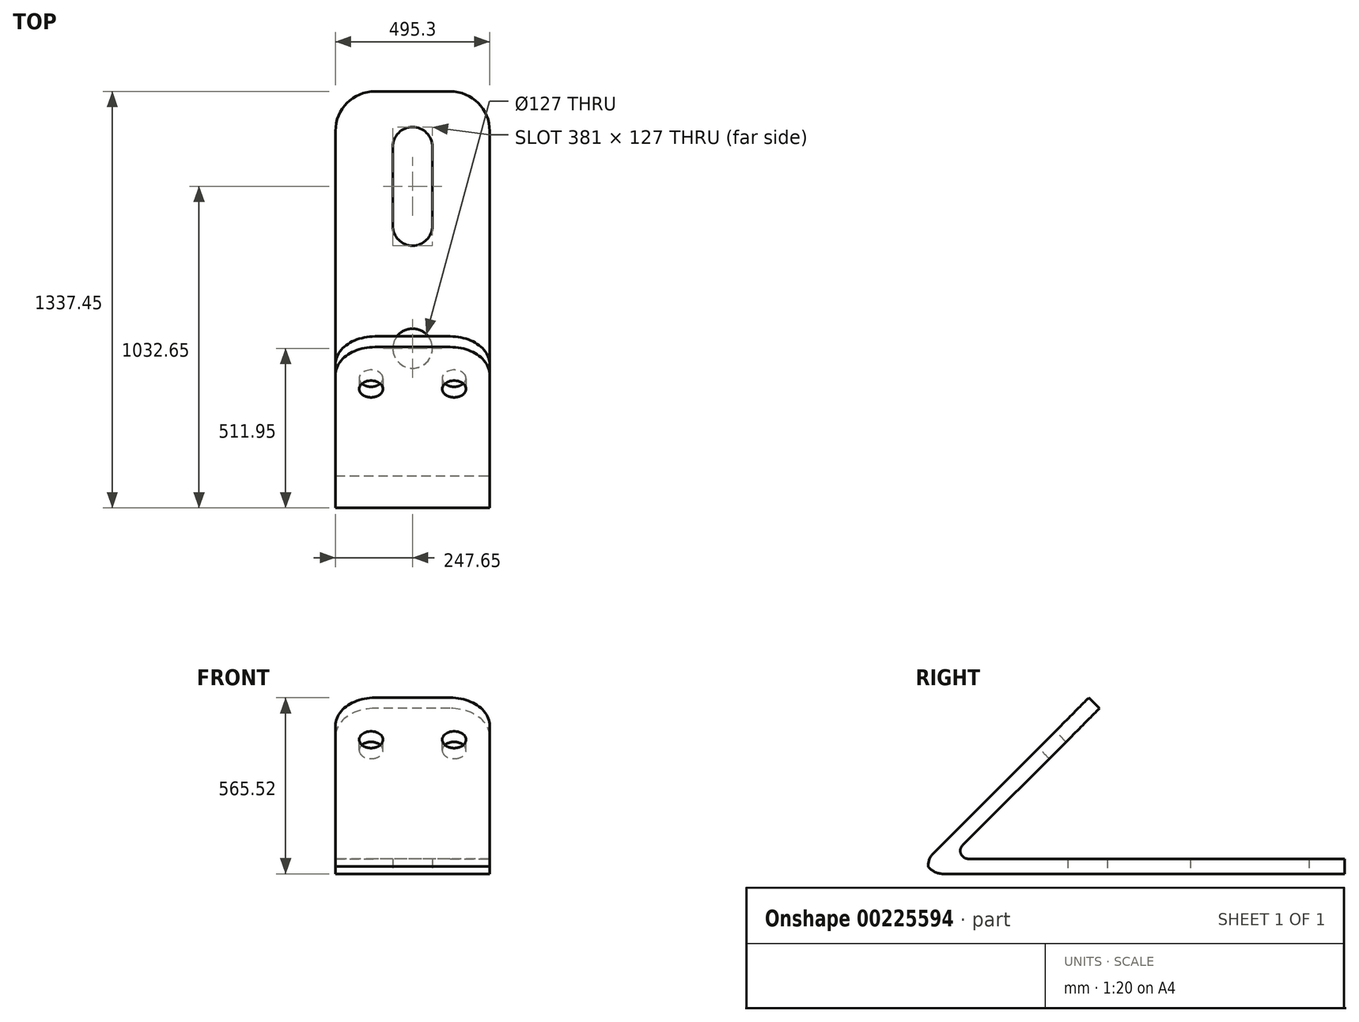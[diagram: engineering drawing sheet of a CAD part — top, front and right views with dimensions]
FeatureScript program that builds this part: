
annotation { "Feature Type Name" : "Feature", "Feature Type Description" : "" }
export const myFeature = defineFeature(function(context is Context, id is Id, definition is map)
    precondition{}
    {
        {
            var Q0;
            Q0=qCreatedBy(makeId("Right.planeOp"),FACE);
            var sketch = newSketch(context, id + "F0", { "sketchPlane" : qUnion([Q0])});
            skLineSegment(sketch, "E0", {"start": v(0, 0) * mm, "end": v(1270, 0) * mm});
            skLineSegment(sketch, "E1", {"start": v(1270, 0) * mm, "end": v(1270, 48.26) * mm});
            skLineSegment(sketch, "E2", {"start": v(1270, 48.26) * mm, "end": v(0, 48.26) * mm});
            skLineSegment(sketch, "E3", {"start": v(0, 48.26) * mm, "end": v(483.14, 531.4) * mm});
            skLineSegment(sketch, "E4", {"start": v(483.14, 531.4) * mm, "end": v(449.01, 565.52) * mm});
            skLineSegment(sketch, "E5", {"start": v(449.01, 565.52) * mm, "end": v(0, 116.5) * mm});
            skLineSegment(sketch, "E6", {"start": v(0, 116.5) * mm, "end": v(-67.45, 49.06) * mm});
            skLineSegment(sketch, "E7", {"start": v(-67.45, 49.06) * mm, "end": v(-67.45, 0) * mm});
            skLineSegment(sketch, "E8", {"start": v(-67.45, 0) * mm, "end": v(0, 0) * mm});
            skSolve(sketch);
        }
        {
            var Q0;
            Q0 = qSketchRegion(id + "F0", true);
            extrude(context, id + "F1", {"entities" : qUnion([Q0]), "endBound" : BoundingType.SYMMETRIC, "depth" : 495.3 * mm});
        }
        {
            var Q0;
            Q0=makeQuery(id+"F1.opExtrude","CAP_EDGE",EDGE,{"disambiguationData":[OSD([sQuery(id+"F0.wireOp",EDGE,"E4")])],"isStart":false});
            var Q1;
            Q1=makeQuery(id+"F1.opExtrude","CAP_EDGE",EDGE,{"disambiguationData":[OSD([sQuery(id+"F0.wireOp",EDGE,"E4")])],"isStart":true});
            var Q2;
            Q2=makeQuery(id+"F1.opExtrude","CAP_EDGE",EDGE,{"disambiguationData":[OSD([sQuery(id+"F0.wireOp",EDGE,"E1")])],"isStart":false});
            var Q3;
            Q3=makeQuery(id+"F1.opExtrude","CAP_EDGE",EDGE,{"disambiguationData":[OSD([sQuery(id+"F0.wireOp",EDGE,"E1")])],"isStart":true});
            fillet(context, id + "F2", {"entities" : qUnion([Q0, Q1, Q2, Q3]), "radius" : 127 * mm, "tangentPropagation" : true, "allowEdgeOverflow" : false});
        }
        {
            var Q0;
            Q0=makeQuery(id+"F1.opExtrude","SWEPT_EDGE",EDGE,{"disambiguationData":[OSD([sQuery(id+"F0.wireOp",EDGE,"E2"),sQuery(id+"F0.wireOp",EDGE,"E3")])]});
            fillet(context, id + "F3", {"entities" : qUnion([Q0]), "radius" : 25.4 * mm, "tangentPropagation" : true, "allowEdgeOverflow" : false});
        }
        {
            var Q0;
            Q0=makeQuery(id+"F1.opExtrude","SWEPT_EDGE",EDGE,{"disambiguationData":[OSD([sQuery(id+"F0.wireOp",EDGE,"E6"),sQuery(id+"F0.wireOp",EDGE,"E7")])]});
            fillet(context, id + "F4", {"entities" : qUnion([Q0]), "radius" : 60.96 * mm, "tangentPropagation" : true, "allowEdgeOverflow" : false});
        }
        {
            var Q0;
            Q0=makeQuery(id+"F1.opExtrude","SWEPT_EDGE",EDGE,{"disambiguationData":[OSD([sQuery(id+"F0.wireOp",EDGE,"E7"),sQuery(id+"F0.wireOp",EDGE,"E8")])]});
            fillet(context, id + "F5", {"entities" : qUnion([Q0]), "radius" : 60.96 * mm, "tangentPropagation" : true, "allowEdgeOverflow" : false});
        }
        {
            var Q0;
            Q0=makeQuery(id+"F1.opExtrude","SWEPT_FACE",FACE,{"disambiguationData":[OSD([sQuery(id+"F0.wireOp",EDGE,"E5"),sQuery(id+"F0.wireOp",EDGE,"E6")])]});
            var sketch = newSketch(context, id + "F6", { "sketchPlane" : qUnion([Q0])});
            skCircle(sketch, "E9", {"center": v(-133.35, 526.88) * mm, "radius": 38.1 * mm});
            skCircle(sketch, "E10", {"center": v(133.35, 526.88) * mm, "radius": 38.1 * mm});
            skSolve(sketch);
        }
        {
            var Q0;
            Q0 = qSketchRegion(id + "F6", true);
            extrude(context, id + "F7", {"entities" : qUnion([Q0]), "operationType" : NewBodyOperationType.REMOVE, "oppositeDirection" : true, "depth" : 132.08 * mm});
        }
        {
            var Q0;
            Q0=qCreatedBy(makeId("Top.planeOp"),FACE);
            var sketch = newSketch(context, id + "F8", { "sketchPlane" : qUnion([Q0])});
            skCircle(sketch, "E11", {"center": v(0, 444.5) * mm, "radius": 63.5 * mm});
            skCircle(sketch, "E12", {"center": v(0, 838.2) * mm, "radius": 63.5 * mm});
            skCircle(sketch, "E13", {"center": v(0, 1092.2) * mm, "radius": 63.5 * mm});
            skLineSegment(sketch, "E14", {"start": v(63.5, 838.2) * mm, "end": v(-63.5, 838.2) * mm});
            skLineSegment(sketch, "E15", {"start": v(-63.5, 838.2) * mm, "end": v(-63.5, 1092.2) * mm});
            skLineSegment(sketch, "E16", {"start": v(-63.5, 1092.2) * mm, "end": v(63.5, 1092.2) * mm});
            skLineSegment(sketch, "E17", {"start": v(63.5, 1092.2) * mm, "end": v(63.5, 838.2) * mm});
            skSolve(sketch);
        }
        {
            var Q0;
            Q0 = qSketchRegion(id + "F8", true);
            extrude(context, id + "F9", {"entities" : qUnion([Q0]), "operationType" : NewBodyOperationType.REMOVE, "depth" : 111.76 * mm});
        }
    });
